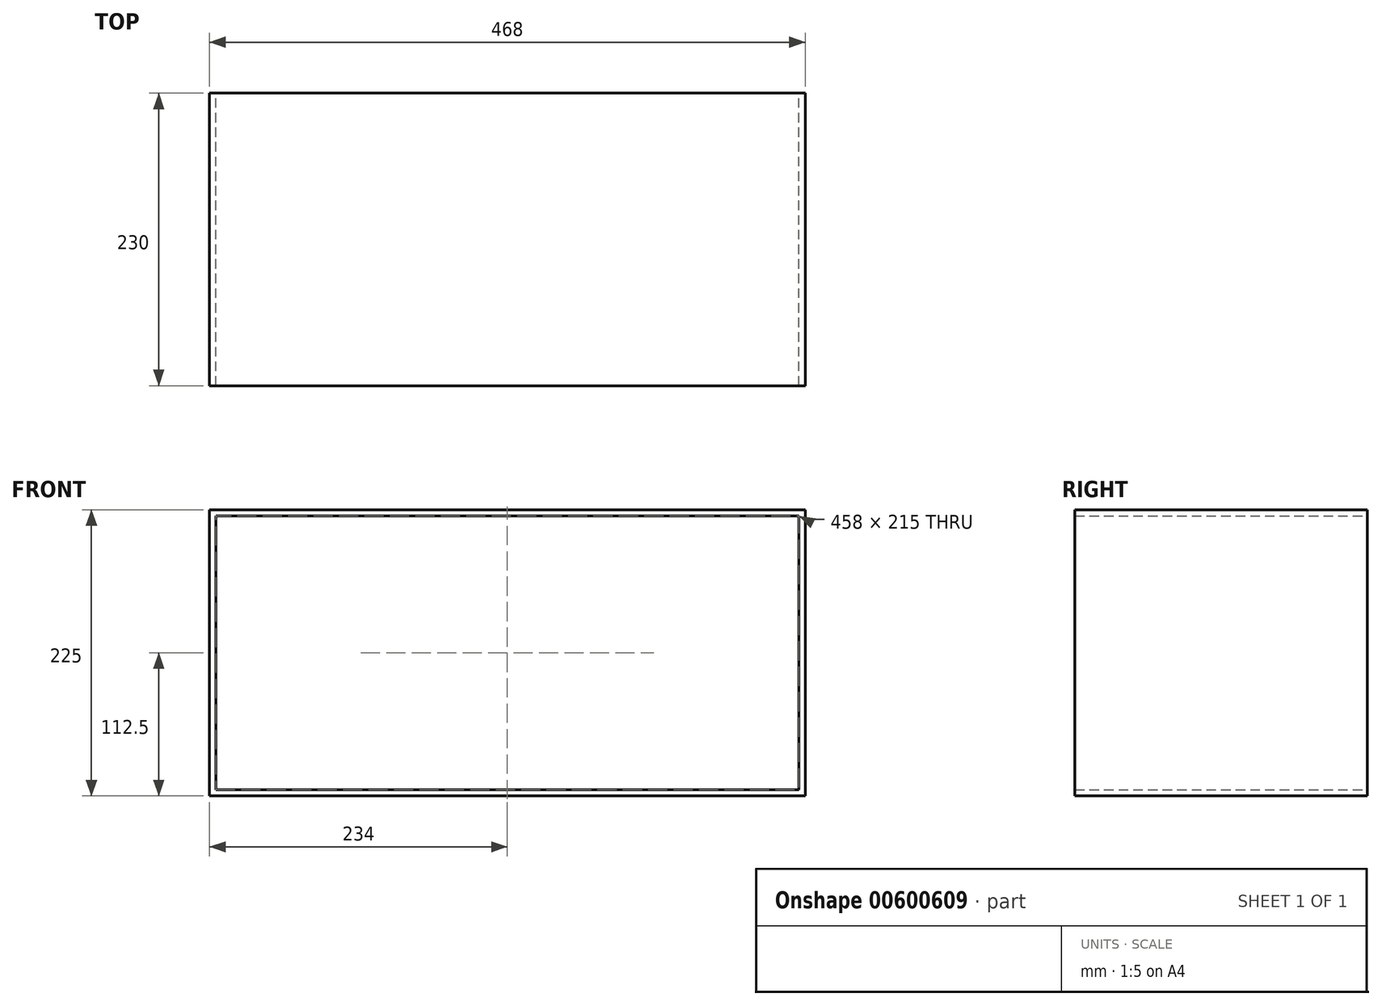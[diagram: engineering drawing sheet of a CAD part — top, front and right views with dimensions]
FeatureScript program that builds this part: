
annotation { "Feature Type Name" : "Feature", "Feature Type Description" : "" }
export const myFeature = defineFeature(function(context is Context, id is Id, definition is map)
    precondition{}
    {
        {
            var Q0;
            Q0=qCreatedBy(makeId("Front.planeOp"),FACE);
            var sketch = newSketch(context, id + "F0", { "sketchPlane" : qUnion([Q0])});
            skLineSegment(sketch, "E0.bottom", {"start": v(229, -107.5) * mm, "end": v(-229, -107.5) * mm});
            skLineSegment(sketch, "E0.top", {"start": v(229, 107.5) * mm, "end": v(-229, 107.5) * mm});
            skLineSegment(sketch, "E0.left", {"start": v(229, -107.5) * mm, "end": v(229, 107.5) * mm});
            skLineSegment(sketch, "E0.right", {"start": v(-229, -107.5) * mm, "end": v(-229, 107.5) * mm});
            skPoint(sketch, "E0.middle", {"position": v(0, 0) * mm});
            skLineSegment(sketch, "E1.0", {"start": v(234, 112.5) * mm, "end": v(-234, 112.5) * mm});
            skLineSegment(sketch, "E1.1", {"start": v(234, -112.5) * mm, "end": v(234, 112.5) * mm});
            skLineSegment(sketch, "E1.2", {"start": v(234, -112.5) * mm, "end": v(-234, -112.5) * mm});
            skLineSegment(sketch, "E1.3", {"start": v(-234, -112.5) * mm, "end": v(-234, 112.5) * mm});
            skSolve(sketch);
        }
        {
            var Q0;
            Q0=makeQuery(id+"F0.imprint","IMPRINT",FACE,{"disambiguationData":[TD([[makeQuery(id+"F0.imprint","IMPRINT",EDGE,{"derivedFrom":sQuery(id+"F0.wireOp",EDGE,"E0.bottom")}),1.0]])]});
            extrude(context, id + "F1", {"entities" : qUnion([Q0]), "depth" : 230 * mm, "offsetDistance" : 25 * mm});
        }
    });
